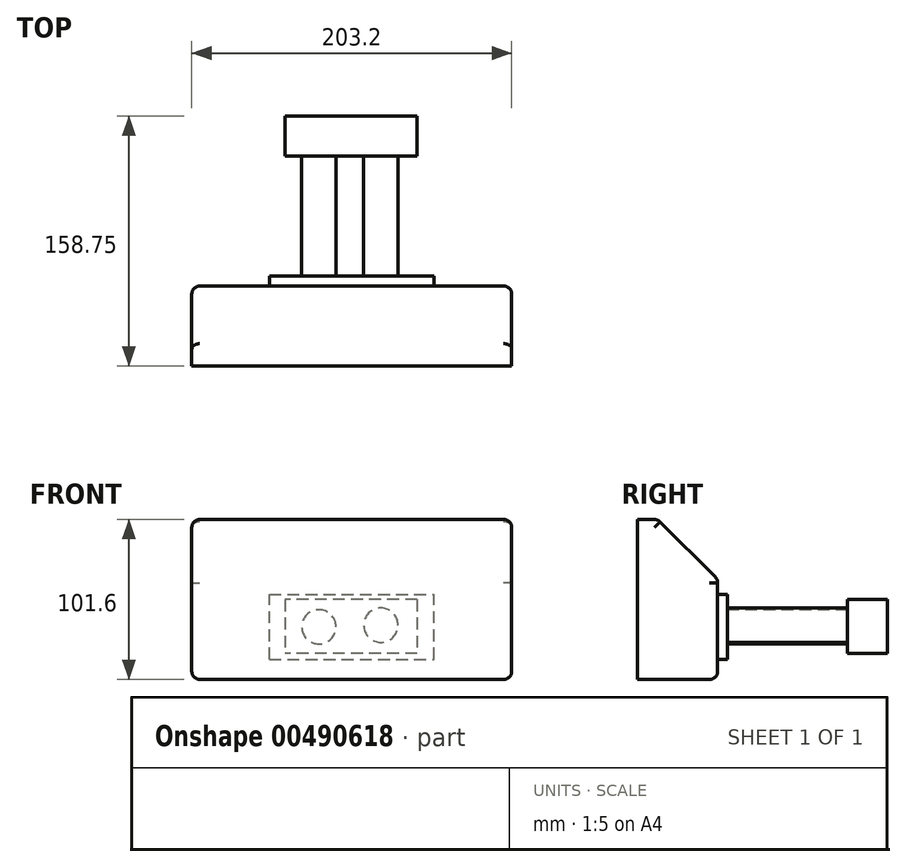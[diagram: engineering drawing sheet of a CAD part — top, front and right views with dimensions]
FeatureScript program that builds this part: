
annotation { "Feature Type Name" : "Feature", "Feature Type Description" : "" }
export const myFeature = defineFeature(function(context is Context, id is Id, definition is map)
    precondition{}
    {
        {
            var Q0;
            Q0=qCreatedBy(makeId("Front.planeOp"),FACE);
            var sketch = newSketch(context, id + "F0", { "sketchPlane" : qUnion([Q0])});
            skLineSegment(sketch, "E0.bottom", {"start": v(-101.6, 50.8) * mm, "end": v(101.6, 50.8) * mm});
            skLineSegment(sketch, "E0.top", {"start": v(-101.6, -50.8) * mm, "end": v(101.6, -50.8) * mm});
            skLineSegment(sketch, "E0.left", {"start": v(-101.6, 50.8) * mm, "end": v(-101.6, -50.8) * mm});
            skLineSegment(sketch, "E0.right", {"start": v(101.6, 50.8) * mm, "end": v(101.6, -50.8) * mm});
            skPoint(sketch, "E0.middle", {"position": v(0, 0) * mm});
            skSolve(sketch);
        }
        {
            var Q0;
            Q0=makeQuery(id+"F0.imprint","IMPRINT",FACE,{"disambiguationData":[TD([[makeQuery(id+"F0.imprint","IMPRINT",EDGE,{"derivedFrom":sQuery(id+"F0.wireOp",EDGE,"E0.bottom")}),-1.0]])]});
            extrude(context, id + "F1", {"entities" : qUnion([Q0]), "depth" : 50.8 * mm});
        }
        {
            var Q0;
            Q0=makeQuery(id+"F1.opExtrude","CAP_EDGE",EDGE,{"disambiguationData":[OSD([sQuery(id+"F0.wireOp",EDGE,"E0.top")])],"isStart":true});
            fillet(context, id + "F2", {"entities" : qUnion([Q0]), "radius" : 5.08 * mm, "tangentPropagation" : true, "allowEdgeOverflow" : false});
        }
        {
            var Q0;
            Q0=makeQuery(id+"F1.opExtrude","CAP_EDGE",EDGE,{"disambiguationData":[OSD([sQuery(id+"F0.wireOp",EDGE,"E0.bottom")])],"isStart":true});
            chamfer(context, id + "F3", {"entities" : qUnion([Q0]), "width" : 38.1 * mm, "tangentPropagation" : true});
        }
        {
            var Q0;
            Q0=makeQuery(id+"F1.opExtrude","CAP_EDGE",EDGE,{"disambiguationData":[OSD([sQuery(id+"F0.wireOp",EDGE,"E0.left")])],"isStart":true});
            fillet(context, id + "F4", {"entities" : qUnion([Q0]), "radius" : 5.08 * mm, "tangentPropagation" : true, "allowEdgeOverflow" : false});
        }
        {
            var Q0;
            Q0=makeQuery(id+"F1.opExtrude","CAP_EDGE",EDGE,{"disambiguationData":[OSD([sQuery(id+"F0.wireOp",EDGE,"E0.right")])],"isStart":true});
            fillet(context, id + "F5", {"entities" : qUnion([Q0]), "radius" : 5.08 * mm, "tangentPropagation" : true, "allowEdgeOverflow" : false});
        }
        {
            var Q0;
            Q0=makeQuery(id+"F3.opChamfer","BLEND_EDGE",EDGE,{"blendedFrom":[makeQuery(id+"F1.opExtrude","CAP_EDGE",EDGE,{"disambiguationData":[OSD([sQuery(id+"F0.wireOp",EDGE,"E0.bottom")])],"isStart":true}),makeQuery(id+"F1.opExtrude","SWEPT_FACE",FACE,{"disambiguationData":[OSD([sQuery(id+"F0.wireOp",EDGE,"E0.right")])]})],"blendedInto":[makeQuery(id+"F1.opExtrude","SWEPT_FACE",FACE,{"disambiguationData":[OSD([sQuery(id+"F0.wireOp",EDGE,"E0.right")])]})]});
            fillet(context, id + "F6", {"entities" : qUnion([Q0]), "radius" : 5.08 * mm, "tangentPropagation" : true, "allowEdgeOverflow" : false});
        }
        {
            var Q0;
            {var subQ0=sQuery(id+"F0.wireOp",EDGE,"E0.bottom");Q0=makeQuery(id+"F3.opChamfer","BLEND_EDGE",EDGE,{"blendedFrom":[makeQuery(id+"F1.opExtrude","CAP_EDGE",EDGE,{"disambiguationData":[OSD([subQ0])],"isStart":true}),makeQuery(id+"F1.opExtrude","SWEPT_FACE",FACE,{"disambiguationData":[OSD([subQ0])]})],"blendedInto":[makeQuery(id+"F1.opExtrude","SWEPT_FACE",FACE,{"disambiguationData":[OSD([subQ0])]})]});}
            fillet(context, id + "F7", {"entities" : qUnion([Q0]), "radius" : 5.08 * mm, "tangentPropagation" : true, "allowEdgeOverflow" : false});
        }
        {
            var Q0;
            Q0=makeQuery(id+"F1.opExtrude","CAP_FACE",FACE,{"disambiguationData":[OSD([sQuery(id+"F0.wireOp",EDGE,"E0.bottom"),sQuery(id+"F0.wireOp",EDGE,"E0.top"),sQuery(id+"F0.wireOp",EDGE,"E0.left"),sQuery(id+"F0.wireOp",EDGE,"E0.right")])],"isStart":true});
            var sketch = newSketch(context, id + "F8", { "sketchPlane" : qUnion([Q0])});
            skLineSegment(sketch, "E1.bottom", {"start": v(52.36, -38.05) * mm, "end": v(-52.36, -38.05) * mm});
            skLineSegment(sketch, "E1.top", {"start": v(52.36, 3.06) * mm, "end": v(-52.36, 3.06) * mm});
            skLineSegment(sketch, "E1.left", {"start": v(52.36, -38.05) * mm, "end": v(52.36, 3.06) * mm});
            skLineSegment(sketch, "E1.right", {"start": v(-52.36, -38.05) * mm, "end": v(-52.36, 3.06) * mm});
            skPoint(sketch, "E1.middle", {"position": v(0, -17.5) * mm});
            skSolve(sketch);
        }
        {
            var Q0;
            Q0 = qSketchRegion(id + "F8", true);
            extrude(context, id + "F9", {"entities" : qUnion([Q0]), "operationType" : NewBodyOperationType.ADD, "depth" : 6.35 * mm});
        }
        {
            var Q0;
            Q0=makeQuery(id+"F9.opExtrude","CAP_FACE",FACE,{"disambiguationData":[OSD([sQuery(id+"F8.wireOp",EDGE,"E1.bottom"),sQuery(id+"F8.wireOp",EDGE,"E1.top"),sQuery(id+"F8.wireOp",EDGE,"E1.left"),sQuery(id+"F8.wireOp",EDGE,"E1.right")])],"isStart":false});
            var sketch = newSketch(context, id + "F10", { "sketchPlane" : qUnion([Q0])});
            skCircle(sketch, "E2", {"center": v(20.87, -17.4) * mm, "radius": 10.9 * mm});
            skCircle(sketch, "E3", {"center": v(-18.5, -16.34) * mm, "radius": 10.9 * mm});
            skSolve(sketch);
        }
        {
            var Q0;
            Q0=makeQuery(id+"F10.imprint","IMPRINT",FACE,{"disambiguationData":[TD([[makeQuery(id+"F10.imprint","IMPRINT",EDGE,{"derivedFrom":sQuery(id+"F10.wireOp",EDGE,"E3")}),1.0]])]});
            var Q1;
            Q1=makeQuery(id+"F10.imprint","IMPRINT",FACE,{"disambiguationData":[TD([[makeQuery(id+"F10.imprint","IMPRINT",EDGE,{"derivedFrom":sQuery(id+"F10.wireOp",EDGE,"E2")}),1.0]])]});
            extrude(context, id + "F11", {"entities" : qUnion([Q0, Q1]), "operationType" : NewBodyOperationType.ADD, "depth" : 76.2 * mm});
        }
        {
            var Q0;
            Q0=makeQuery(id+"F11.opExtrude","CAP_FACE",FACE,{"disambiguationData":[OSD([sQuery(id+"F10.wireOp",EDGE,"E3")])],"isStart":false});
            var sketch = newSketch(context, id + "F12", { "sketchPlane" : qUnion([Q0])});
            skLineSegment(sketch, "E4.bottom", {"start": v(-41.54, 0) * mm, "end": v(42.4, 0) * mm});
            skLineSegment(sketch, "E4.top", {"start": v(-41.54, -34.39) * mm, "end": v(42.4, -34.39) * mm});
            skLineSegment(sketch, "E4.left", {"start": v(-41.54, 0) * mm, "end": v(-41.54, -34.39) * mm});
            skLineSegment(sketch, "E4.right", {"start": v(42.4, 0) * mm, "end": v(42.4, -34.39) * mm});
            skSolve(sketch);
        }
        {
            var Q0;
            Q0 = qSketchRegion(id + "F12", true);
            extrude(context, id + "F13", {"entities" : qUnion([Q0]), "operationType" : NewBodyOperationType.ADD, "depth" : 25.4 * mm});
        }
    });
